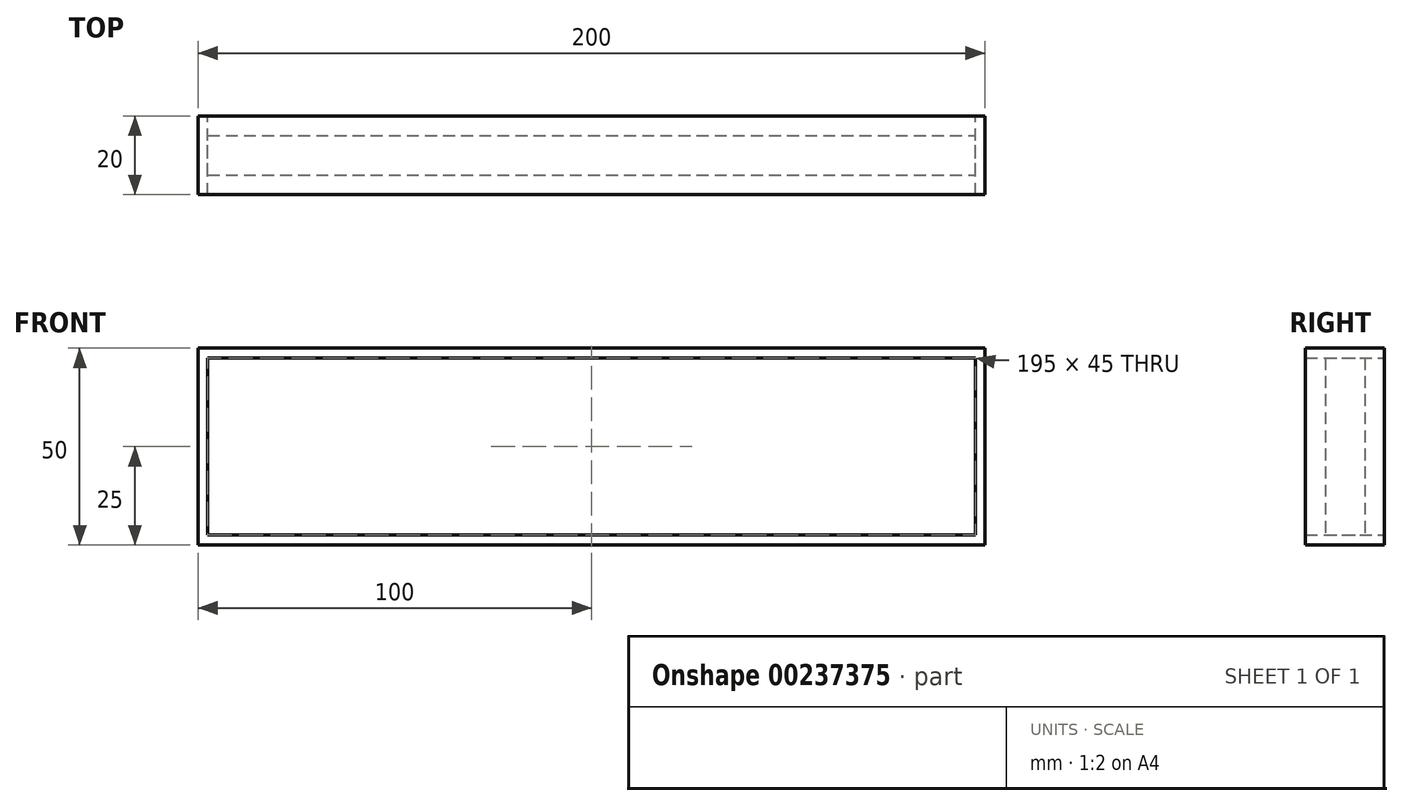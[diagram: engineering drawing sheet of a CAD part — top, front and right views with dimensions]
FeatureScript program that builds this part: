
annotation { "Feature Type Name" : "Feature", "Feature Type Description" : "" }
export const myFeature = defineFeature(function(context is Context, id is Id, definition is map)
    precondition{}
    {
        {
            var Q0;
            Q0=qCreatedBy(makeId("Front.planeOp"),FACE);
            var sketch = newSketch(context, id + "F0", { "sketchPlane" : qUnion([Q0])});
            skLineSegment(sketch, "E0.bottom", {"start": v(0, 0) * mm, "end": v(200, 0) * mm});
            skLineSegment(sketch, "E0.top", {"start": v(0, -50) * mm, "end": v(200, -50) * mm});
            skLineSegment(sketch, "E0.left", {"start": v(0, 0) * mm, "end": v(0, -50) * mm});
            skLineSegment(sketch, "E0.right", {"start": v(200, 0) * mm, "end": v(200, -50) * mm});
            skLineSegment(sketch, "E1.bottom", {"start": v(0, 0) * mm, "end": v(2.5, 0) * mm});
            skLineSegment(sketch, "E1.left", {"start": v(0, 0) * mm, "end": v(0, -2.5) * mm});
            skLineSegment(sketch, "E2.bottom", {"start": v(200, -50) * mm, "end": v(197.5, -50) * mm});
            skLineSegment(sketch, "E2.left", {"start": v(200, -50) * mm, "end": v(200, -47.5) * mm});
            skLineSegment(sketch, "E3.bottom", {"start": v(2.5, -2.5) * mm, "end": v(197.5, -2.5) * mm});
            skLineSegment(sketch, "E3.top", {"start": v(2.5, -47.5) * mm, "end": v(197.5, -47.5) * mm});
            skLineSegment(sketch, "E3.left", {"start": v(2.5, -2.5) * mm, "end": v(2.5, -47.5) * mm});
            skLineSegment(sketch, "E3.right", {"start": v(197.5, -2.5) * mm, "end": v(197.5, -47.5) * mm});
            skSolve(sketch);
        }
        {
            var Q0;
            Q0=makeQuery(id+"F0.imprint","IMPRINT",FACE,{"disambiguationData":[TD([[makeQuery(id+"F0.imprint","IMPRINT",EDGE,{"derivedFrom":sQuery(id+"F0.wireOp",EDGE,"E0.bottom")}),-1.0]])]});
            extrude(context, id + "F1", {"entities" : qUnion([Q0]), "depth" : 10 * mm, "hasSecondDirection" : true, "secondDirectionOppositeDirection" : true, "secondDirectionDepth" : 10 * mm});
        }
        {
            var Q0;
            Q0=makeQuery(id+"F0.imprint","IMPRINT",FACE,{"disambiguationData":[TD([[makeQuery(id+"F0.imprint","IMPRINT",EDGE,{"derivedFrom":sQuery(id+"F0.wireOp",EDGE,"E3.bottom")}),-1.0]])]});
            extrude(context, id + "F2", {"entities" : qUnion([Q0]), "depth" : 5 * mm, "hasSecondDirection" : true, "secondDirectionOppositeDirection" : true, "secondDirectionDepth" : 5 * mm});
        }
    });
